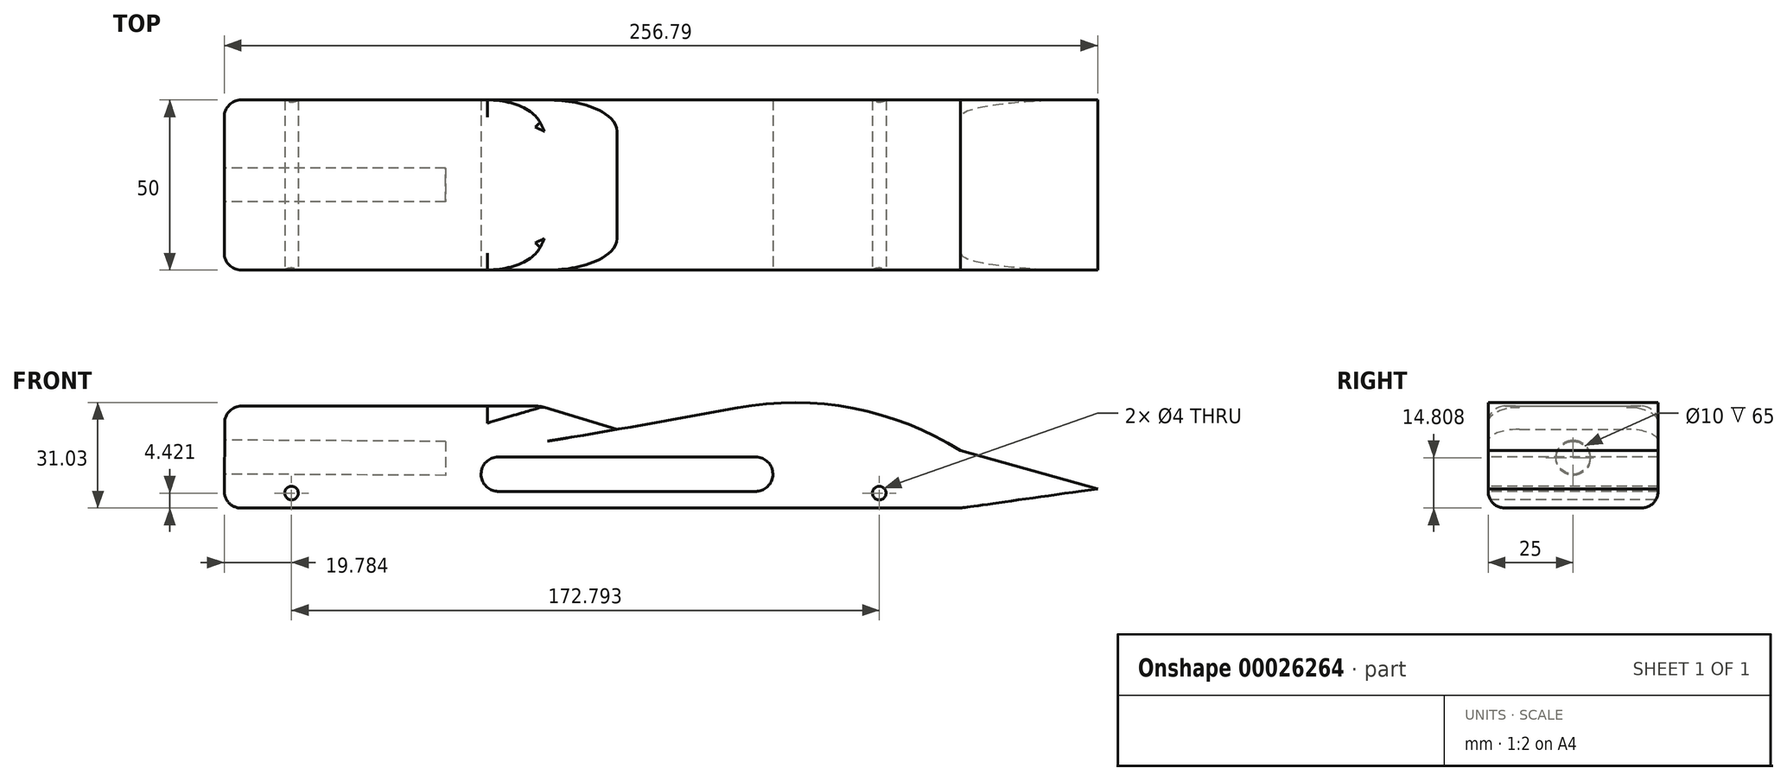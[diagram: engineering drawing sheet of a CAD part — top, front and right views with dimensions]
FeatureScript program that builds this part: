
annotation { "Feature Type Name" : "Feature", "Feature Type Description" : "" }
export const myFeature = defineFeature(function(context is Context, id is Id, definition is map)
    precondition{}
    {
        {
            var Q0;
            Q0=qCreatedBy(makeId("Front.planeOp"),FACE);
            var sketch = newSketch(context, id + "F0", { "sketchPlane" : qUnion([Q0])});
            skLineSegment(sketch, "E0", {"start": v(-84.2, -32.3) * mm, "end": v(132.25, -32.3) * mm});
            skLineSegment(sketch, "E1", {"start": v(132.25, -32.3) * mm, "end": v(172.62, -26.62) * mm});
            skLineSegment(sketch, "E2", {"start": v(172.62, -26.62) * mm, "end": v(132.25, -15.42) * mm});
            skArc(sketch, "E3", {"start": v(132.25, -15.42) * mm, "mid": v(94.9, -2) * mm, "end": v(55.36, -5.66) * mm});
            skLineSegment(sketch, "E4", {"start": v(55.36, -5.66) * mm, "end": v(44.56, -9.14) * mm});
            skLineSegment(sketch, "E5", {"start": v(31.35, -9.14) * mm, "end": v(44.56, -9.14) * mm});
            skLineSegment(sketch, "E6", {"start": v(31.35, -9.14) * mm, "end": v(8.66, -2.3) * mm});
            skLineSegment(sketch, "E7", {"start": v(8.66, -2.3) * mm, "end": v(-84.02, -2.3) * mm});
            skLineSegment(sketch, "E8", {"start": v(-84.02, -2.3) * mm, "end": v(-84.2, -32.3) * mm});
            skSolve(sketch);
        }
        {
            var Q0;
            Q0 = qSketchRegion(id + "F0", true);
            extrude(context, id + "F1", {"entities" : qUnion([Q0]), "depth" : 50 * mm});
        }
        {
            var Q0;
            Q0=makeQuery(id+"F1.opExtrude","SWEPT_FACE",FACE,{"disambiguationData":[OSD([sQuery(id+"F0.wireOp",EDGE,"E8")])]});
            var sketch = newSketch(context, id + "F2", { "sketchPlane" : qUnion([Q0])});
            skCircle(sketch, "E9", {"center": v(25, -17.8) * mm, "radius": 5 * mm});
            skSolve(sketch);
        }
        {
            var Q0;
            Q0 = qSketchRegion(id + "F2", true);
            extrude(context, id + "F3", {"entities" : qUnion([Q0]), "operationType" : NewBodyOperationType.REMOVE, "oppositeDirection" : true, "depth" : 65 * mm});
        }
        {
            var Q0;
            Q0=makeQuery(id+"F1.opExtrude","SWEPT_EDGE",EDGE,{"disambiguationData":[OSD([sQuery(id+"F0.wireOp",EDGE,"E4"),sQuery(id+"F0.wireOp",EDGE,"E5")])]});
            fillet(context, id + "F4", {"entities" : qUnion([Q0]), "radius" : 3268.26 * mm, "tangentPropagation" : true, "allowEdgeOverflow" : false});
        }
        {
            var Q0;
            Q0=makeQuery(id+"F1.opExtrude","CAP_FACE",FACE,{"disambiguationData":[OSD([sQuery(id+"F0.wireOp",EDGE,"E0"),sQuery(id+"F0.wireOp",EDGE,"E1"),sQuery(id+"F0.wireOp",EDGE,"E2"),sQuery(id+"F0.wireOp",EDGE,"E3"),sQuery(id+"F0.wireOp",EDGE,"E4"),sQuery(id+"F0.wireOp",EDGE,"E5"),sQuery(id+"F0.wireOp",EDGE,"E6"),sQuery(id+"F0.wireOp",EDGE,"E7"),sQuery(id+"F0.wireOp",EDGE,"E8")])],"isStart":false});
            var sketch = newSketch(context, id + "F5", { "sketchPlane" : qUnion([Q0])});
            skCircle(sketch, "E10", {"center": v(-64.39, -27.88) * mm, "radius": 2 * mm});
            skCircle(sketch, "E11", {"center": v(108.4, -27.88) * mm, "radius": 2 * mm});
            skSolve(sketch);
        }
        {
            var Q0;
            Q0 = qSketchRegion(id + "F5", true);
            extrude(context, id + "F6", {"entities" : qUnion([Q0]), "operationType" : NewBodyOperationType.REMOVE, "endBound" : BoundingType.THROUGH_ALL, "oppositeDirection" : true, "depth" : 25 * mm});
        }
        {
            var Q0;
            Q0=makeQuery(id+"F1.opExtrude","CAP_EDGE",EDGE,{"disambiguationData":[OSD([sQuery(id+"F0.wireOp",EDGE,"E7")])],"isStart":false});
            fillet(context, id + "F7", {"entities" : qUnion([Q0]), "radius" : 5 * mm, "tangentPropagation" : true, "allowEdgeOverflow" : false});
        }
        {
            var Q0;
            Q0=makeQuery(id+"F1.opExtrude","CAP_EDGE",EDGE,{"disambiguationData":[OSD([sQuery(id+"F0.wireOp",EDGE,"E7")])],"isStart":true});
            var Q1;
            Q1=makeQuery(id+"F1.opExtrude","SWEPT_EDGE",EDGE,{"disambiguationData":[OSD([sQuery(id+"F0.wireOp",EDGE,"E7"),sQuery(id+"F0.wireOp",EDGE,"E8")])]});
            var Q2;
            Q2=makeQuery(id+"F1.opExtrude","CAP_EDGE",EDGE,{"disambiguationData":[OSD([sQuery(id+"F0.wireOp",EDGE,"E8")])],"isStart":true});
            fillet(context, id + "F8", {"entities" : qUnion([Q0, Q1, Q2]), "radius" : 5 * mm, "tangentPropagation" : true, "allowEdgeOverflow" : false});
        }
        {
            var Q0;
            Q0=makeQuery(id+"F1.opExtrude","SWEPT_EDGE",EDGE,{"disambiguationData":[OSD([sQuery(id+"F0.wireOp",EDGE,"E6"),sQuery(id+"F0.wireOp",EDGE,"E7")])]});
            fillet(context, id + "F9", {"entities" : qUnion([Q0]), "radius" : 9.25 * mm, "tangentPropagation" : true, "allowEdgeOverflow" : false});
        }
        {
            var Q0;
            Q0=makeQuery(id+"F1.opExtrude","CAP_FACE",FACE,{"disambiguationData":[OSD([sQuery(id+"F0.wireOp",EDGE,"E0"),sQuery(id+"F0.wireOp",EDGE,"E1"),sQuery(id+"F0.wireOp",EDGE,"E2"),sQuery(id+"F0.wireOp",EDGE,"E3"),sQuery(id+"F0.wireOp",EDGE,"E4"),sQuery(id+"F0.wireOp",EDGE,"E5"),sQuery(id+"F0.wireOp",EDGE,"E6"),sQuery(id+"F0.wireOp",EDGE,"E7"),sQuery(id+"F0.wireOp",EDGE,"E8")])],"isStart":false});
            var sketch = newSketch(context, id + "F10", { "sketchPlane" : qUnion([Q0])});
            skLineSegment(sketch, "E12", {"start": v(-8.64, -17.28) * mm, "end": v(-8.64, -27.37) * mm});
            skLineSegment(sketch, "E13", {"start": v(-8.64, -17.28) * mm, "end": v(77.13, -17.28) * mm});
            skLineSegment(sketch, "E14", {"start": v(-8.64, -27.37) * mm, "end": v(77.13, -27.37) * mm});
            skLineSegment(sketch, "E15", {"start": v(77.13, -17.28) * mm, "end": v(77.13, -27.37) * mm});
            skSolve(sketch);
        }
        {
            var Q0;
            Q0 = qSketchRegion(id + "F10", true);
            extrude(context, id + "F11", {"entities" : qUnion([Q0]), "operationType" : NewBodyOperationType.REMOVE, "endBound" : BoundingType.THROUGH_ALL, "oppositeDirection" : true, "depth" : 25 * mm});
        }
        {
            var Q0;
            Q0=makeQuery(id+"F11.boolean.opBoolean","COPY",EDGE,{"derivedFrom":makeQuery(id+"F11.opExtrude","SWEPT_EDGE",EDGE,{"disambiguationData":[OSD([sQuery(id+"F10.wireOp",EDGE,"E12"),sQuery(id+"F10.wireOp",EDGE,"E14")])]})});
            var Q1;
            Q1=makeQuery(id+"F11.boolean.opBoolean","COPY",EDGE,{"derivedFrom":makeQuery(id+"F11.opExtrude","SWEPT_EDGE",EDGE,{"disambiguationData":[OSD([sQuery(id+"F10.wireOp",EDGE,"E12"),sQuery(id+"F10.wireOp",EDGE,"E13")])]})});
            var Q2;
            Q2=makeQuery(id+"F11.boolean.opBoolean","COPY",EDGE,{"derivedFrom":makeQuery(id+"F11.opExtrude","SWEPT_EDGE",EDGE,{"disambiguationData":[OSD([sQuery(id+"F10.wireOp",EDGE,"E13"),sQuery(id+"F10.wireOp",EDGE,"E15")])]})});
            var Q3;
            Q3=makeQuery(id+"F11.boolean.opBoolean","COPY",EDGE,{"derivedFrom":makeQuery(id+"F11.opExtrude","SWEPT_EDGE",EDGE,{"disambiguationData":[OSD([sQuery(id+"F10.wireOp",EDGE,"E14"),sQuery(id+"F10.wireOp",EDGE,"E15")])]})});
            fillet(context, id + "F12", {"entities" : qUnion([Q0, Q1, Q2, Q3]), "radius" : 5 * mm, "tangentPropagation" : true, "allowEdgeOverflow" : false});
        }
        {
            var Q0;
            Q0=makeQuery(id+"F1.opExtrude","CAP_EDGE",EDGE,{"disambiguationData":[OSD([sQuery(id+"F0.wireOp",EDGE,"E0")])],"isStart":false});
            fillet(context, id + "F13", {"entities" : qUnion([Q0]), "radius" : 5 * mm, "tangentPropagation" : true, "allowEdgeOverflow" : false});
        }
    });
